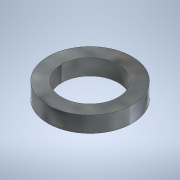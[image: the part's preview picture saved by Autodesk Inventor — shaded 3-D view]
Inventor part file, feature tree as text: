
AUTODESK INVENTOR PART (.ipt)
format: ipt  version: 2022 (Build 260153000, 153)  size: 112,640 bytes
history: native  units: mm
features: other x1, extrude x1, sketch x1
ambient origin geometry x8: Origin, YZ Plane, XZ Plane, XY Plane, X Axis, Y Axis, Z Axis, Center Point
bodies: Body1 (feature_tree)
feature tree (3):
  other  "Твердое тело1"
  extrude  "Выдавливание1"  Depth=37.0mm
  sketch  "Эскиз1"
